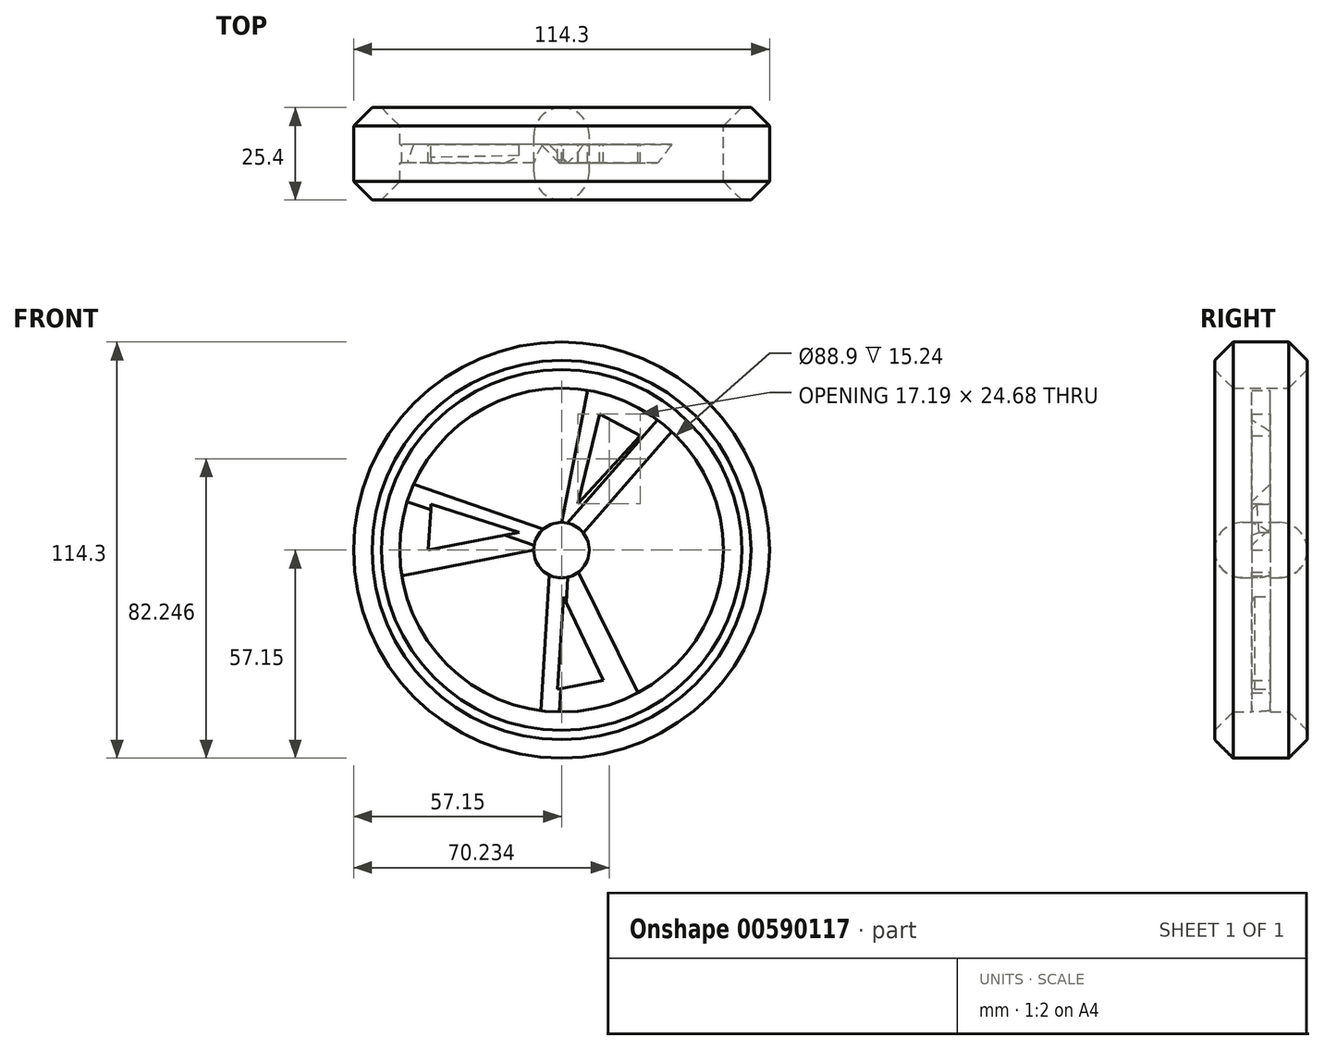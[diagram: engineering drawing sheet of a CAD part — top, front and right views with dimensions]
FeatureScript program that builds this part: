
annotation { "Feature Type Name" : "Feature", "Feature Type Description" : "" }
export const myFeature = defineFeature(function(context is Context, id is Id, definition is map)
    precondition{}
    {
        {
            var Q0;
            Q0=qCreatedBy(makeId("Front.planeOp"),FACE);
            var sketch = newSketch(context, id + "F0", { "sketchPlane" : qUnion([Q0])});
            skCircle(sketch, "E0", {"center": v(0, 0) * mm, "radius": 57.15 * mm});
            skCircle(sketch, "E1", {"center": v(0, 0) * mm, "radius": 44.45 * mm});
            skCircle(sketch, "E2", {"center": v(0, 0) * mm, "radius": 7.62 * mm});
            skLineSegment(sketch, "E3", {"start": v(-3.36, -6.84) * mm, "end": v(-5.65, -44.09) * mm});
            skLineSegment(sketch, "E4", {"start": v(4.57, -6.1) * mm, "end": v(21.04, -39.15) * mm});
            skLineSegment(sketch, "E5", {"start": v(5.98, 4.72) * mm, "end": v(30.3, 32.52) * mm});
            skLineSegment(sketch, "E6", {"start": v(0, 7.62) * mm, "end": v(7.16, 43.87) * mm});
            skLineSegment(sketch, "E7", {"start": v(-4.99, 5.76) * mm, "end": v(-40.62, 18.06) * mm});
            skLineSegment(sketch, "E8", {"start": v(-7.62, 0) * mm, "end": v(-43.9, -7.02) * mm});
            skLineSegment(sketch, "E9", {"start": v(-11.7, 4.83) * mm, "end": v(-35.85, 12.68) * mm});
            skLineSegment(sketch, "E10", {"start": v(-35.85, 12.68) * mm, "end": v(-36.63, 0) * mm});
            skLineSegment(sketch, "E11", {"start": v(-36.63, 0) * mm, "end": v(-11.7, 4.83) * mm});
            skLineSegment(sketch, "E12", {"start": v(0.52, -12.82) * mm, "end": v(-1.04, -38.17) * mm});
            skLineSegment(sketch, "E13", {"start": v(-1.04, -38.17) * mm, "end": v(11.43, -35.76) * mm});
            skLineSegment(sketch, "E14", {"start": v(11.43, -35.76) * mm, "end": v(0.52, -12.82) * mm});
            skLineSegment(sketch, "E15", {"start": v(4.49, 12.75) * mm, "end": v(10.48, 37.44) * mm});
            skLineSegment(sketch, "E16", {"start": v(10.48, 37.44) * mm, "end": v(21.68, 31.45) * mm});
            skLineSegment(sketch, "E17", {"start": v(21.68, 31.45) * mm, "end": v(4.49, 12.75) * mm});
            skSolve(sketch);
        }
        {
            var Q0;
            Q0=makeQuery(id+"F0.imprint","IMPRINT",FACE,{"disambiguationData":[TD([[makeQuery(id+"F0.imprint","IMPRINT",EDGE,{"derivedFrom":sQuery(id+"F0.wireOp",EDGE,"E0")}),1.0]])]});
            var Q1;
            {var subQ0=sQuery(id+"F0.wireOp",EDGE,"E2");var subQ5=makeQuery(id+"F0.imprint","INTERSECT",VERTEX,{"derivedFrom":[subQ0,sQuery(id+"F0.wireOp",EDGE,"E5")]});Q1=makeQuery(id+"F0.imprint","IMPRINT",FACE,{"disambiguationData":[TD([[makeQuery(id+"F0.imprint","IMPRINT",EDGE,{"disambiguationData":[TD([[subQ5,-1.0]])],"derivedFrom":subQ0}),1.0]])]});}
            extrude(context, id + "F1", {"entities" : qUnion([Q0, Q1]), "depth" : 12.7 * mm, "offsetDistance" : 25.4 * mm, "hasSecondDirection" : true, "secondDirectionOppositeDirection" : true, "secondDirectionDepth" : 12.7 * mm});
        }
        {
            var Q0;
            {var subQ0=sQuery(id+"F0.wireOp",EDGE,"E5");Q0=makeQuery(id+"F0.imprint","IMPRINT",FACE,{"disambiguationData":[TD([[makeQuery(id+"F0.imprint","IMPRINT",EDGE,{"derivedFrom":subQ0}),1.0]])]});}
            var Q1;
            {var subQ0=sQuery(id+"F0.wireOp",EDGE,"E7");Q1=makeQuery(id+"F0.imprint","IMPRINT",FACE,{"disambiguationData":[TD([[makeQuery(id+"F0.imprint","IMPRINT",EDGE,{"derivedFrom":subQ0}),1.0]])]});}
            var Q2;
            {var subQ0=sQuery(id+"F0.wireOp",EDGE,"E3");Q2=makeQuery(id+"F0.imprint","IMPRINT",FACE,{"disambiguationData":[TD([[makeQuery(id+"F0.imprint","IMPRINT",EDGE,{"derivedFrom":subQ0}),1.0]])]});}
            extrude(context, id + "F2", {"entities" : qUnion([Q0, Q1, Q2]), "operationType" : NewBodyOperationType.ADD, "depth" : 2.54 * mm, "offsetDistance" : 25.4 * mm, "hasSecondDirection" : true, "secondDirectionOppositeDirection" : true, "secondDirectionDepth" : 2.54 * mm});
        }
        {
            var Q0;
            Q0=makeQuery(id+"F1.opExtrude","CAP_EDGE",EDGE,{"disambiguationData":[OSD([sQuery(id+"F0.wireOp",EDGE,"E2")])],"isStart":false});
            var Q1;
            Q1=makeQuery(id+"F1.opExtrude","CAP_EDGE",EDGE,{"disambiguationData":[OSD([sQuery(id+"F0.wireOp",EDGE,"E2")])],"isStart":true});
            fillet(context, id + "F3", {"entities" : qUnion([Q0, Q1]), "radius" : 7.62 * mm, "tangentPropagation" : true, "allowEdgeOverflow" : false});
        }
        {
            var Q0;
            Q0=makeQuery(id+"F2.opExtrude","CAP_EDGE",EDGE,{"disambiguationData":[OSD([sQuery(id+"F0.wireOp",EDGE,"E7")])],"isStart":false});
            var Q1;
            Q1=makeQuery(id+"F2.opExtrude","CAP_EDGE",EDGE,{"disambiguationData":[OSD([sQuery(id+"F0.wireOp",EDGE,"E5")])],"isStart":false});
            var Q2;
            Q2=makeQuery(id+"F2.opExtrude","CAP_EDGE",EDGE,{"disambiguationData":[OSD([sQuery(id+"F0.wireOp",EDGE,"E3")])],"isStart":false});
            var Q3;
            Q3=makeQuery(id+"F1.opExtrude","CAP_EDGE",EDGE,{"disambiguationData":[OSD([sQuery(id+"F0.wireOp",EDGE,"E1")])],"isStart":false});
            var Q4;
            Q4=makeQuery(id+"F1.opExtrude","CAP_EDGE",EDGE,{"disambiguationData":[OSD([sQuery(id+"F0.wireOp",EDGE,"E1")])],"isStart":true});
            var Q5;
            Q5=makeQuery(id+"F1.opExtrude","CAP_EDGE",EDGE,{"disambiguationData":[OSD([sQuery(id+"F0.wireOp",EDGE,"E0")])],"isStart":true});
            var Q6;
            Q6=makeQuery(id+"F1.opExtrude","CAP_EDGE",EDGE,{"disambiguationData":[OSD([sQuery(id+"F0.wireOp",EDGE,"E0")])],"isStart":false});
            chamfer(context, id + "F4", {"entities" : qUnion([Q0, Q1, Q2, Q3, Q4, Q5, Q6]), "width" : 5.08 * mm, "tangentPropagation" : true});
        }
    });
